MODEL slx_21c90f519a57
CONFIG AbsTol = auto
CONFIG FixedStep = 0.1
CONFIG MaxStep = auto
CONFIG MinStep = auto
CONFIG RelTol = 1e-3
CONFIG SampleTimeConstraint = Unconstrained
CONFIG Solver = ode3
CONFIG SolverMode = Auto
CONFIG SolverName = ode3
CONFIG StartTime = 0.0
CONFIG StopTime = 10.0
BLOCK [Demux] Demux
  DisplayOption = bar
  Outputs = 2
  Ports = [1, 2]
BLOCK [Fcn] Fcn
  Expr = cos(u)
BLOCK [Fcn] Fcn1
  Expr = sin(u)
BLOCK [Integrator] Integrator
  Ports = [1, 1]
BLOCK [Integrator] Integrator1
  Ports = [1, 1]
BLOCK [Integrator] Integrator2
  Ports = [1, 1]
BLOCK [Mux] Mux
  DisplayOption = bar
  Inputs = 3
  Ports = [3, 1]
BLOCK [Product] Product
  InputSameDT = off
  OutDataTypeStr = Inherit: Inherit via internal rule
  Ports = [2, 1]
  RndMeth = Floor
  SaturateOnIntegerOverflow = off
BLOCK [Product] Product1
  InputSameDT = off
  OutDataTypeStr = Inherit: Inherit via internal rule
  Ports = [2, 1]
  RndMeth = Floor
  SaturateOnIntegerOverflow = off
BLOCK [ToWorkspace] To Workspace
  FixptAsFi = on
  MaxDataPoints = inf
  Ports = [1]
  SampleTime = -1
  Save2DSignal = 3-D array (concatenate along third dimension)
  VariableName = h
BLOCK [Constant] invF23
  Value = [r/2, r/2; r/(2*L) -r/(2*L)]
BLOCK [Constant] qm_dot
  Value = qdot
BLOCK [Product] u_m Func
  InputSameDT = off
  Multiplication = Matrix(*)
  OutDataTypeStr = Inherit: Inherit via internal rule
  Ports = [2, 1]
  RndMeth = Floor
  SaturateOnIntegerOverflow = off
LINE Demux:1 -> Product1:1
LINE Demux:1 -> Product:1
LINE Demux:2 -> Integrator:1
LINE Fcn1:1 -> Product1:2
LINE Fcn:1 -> Product:2
LINE Integrator1:1 -> Mux:1
LINE Integrator2:1 -> Mux:2
LINE Integrator:1 -> Fcn1:1
LINE Integrator:1 -> Fcn:1
LINE Integrator:1 -> Mux:3
LINE Mux:1 -> To Workspace:1
LINE Product1:1 -> Integrator2:1
LINE Product:1 -> Integrator1:1
LINE invF23:1 -> u_m Func:1
LINE qm_dot:1 -> u_m Func:2
LINE u_m Func:1 -> Demux:1
